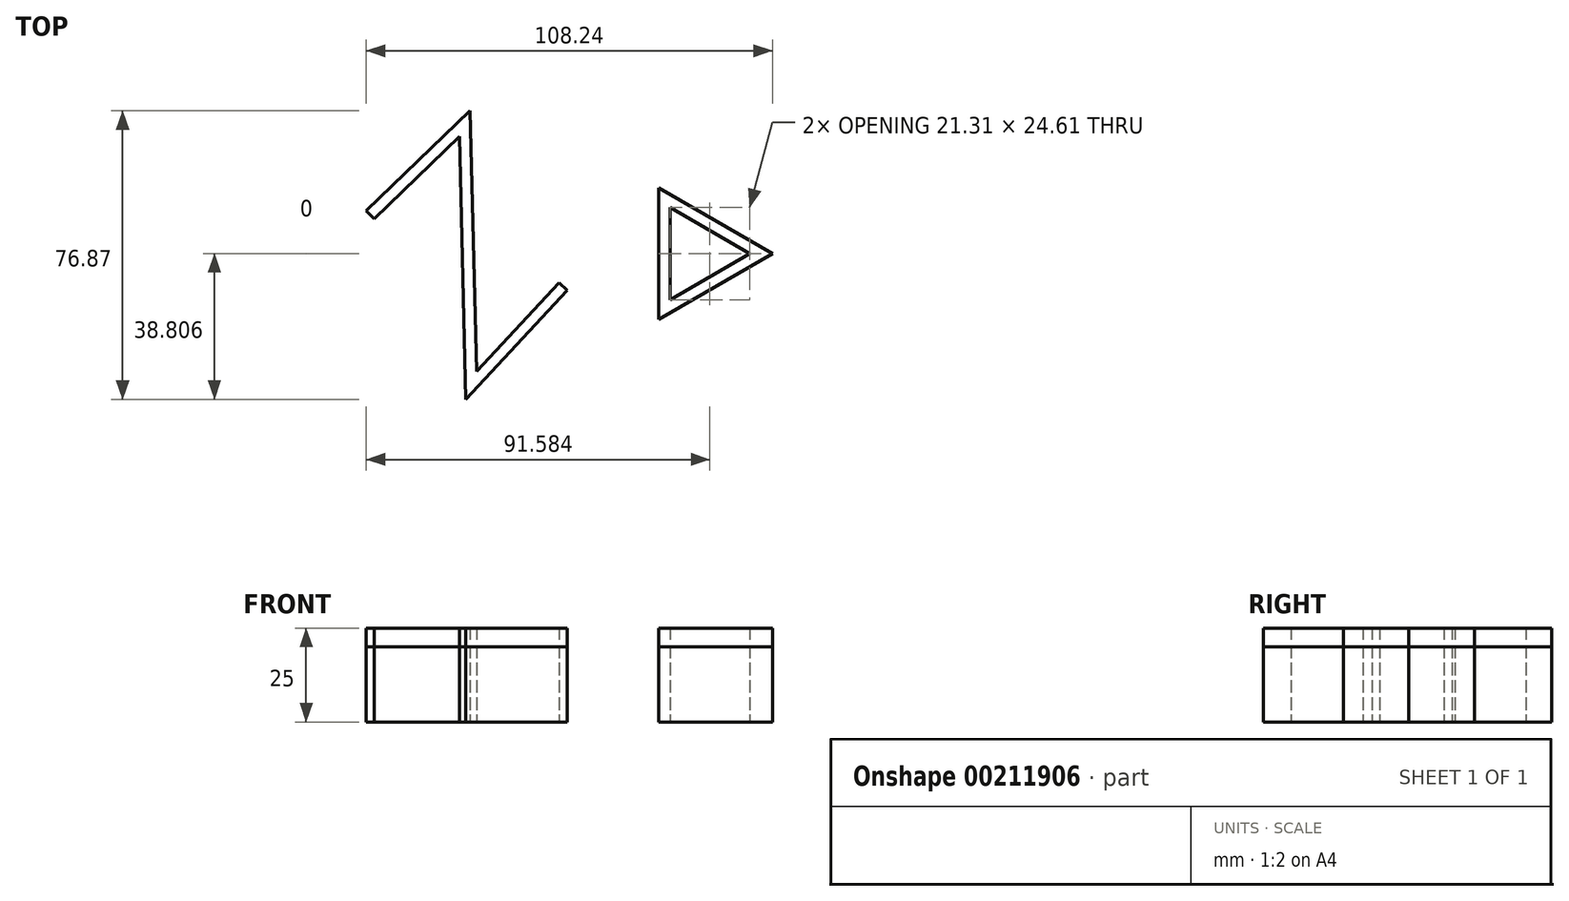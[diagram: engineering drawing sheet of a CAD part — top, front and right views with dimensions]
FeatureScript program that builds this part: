
annotation { "Feature Type Name" : "Feature", "Feature Type Description" : "" }
export const myFeature = defineFeature(function(context is Context, id is Id, definition is map)
    precondition{}
    {
        {
            var Q0;
            Q0=qCreatedBy(makeId("Top.planeOp"),FACE);
            var sketch = newSketch(context, id + "F0", { "sketchPlane" : qUnion([Q0])});
            skCircle(sketch, "E0.cCircle", {"center": v(33.51, 1.03) * mm, "radius": 10.1 * mm, "construction": true});
            skLineSegment(sketch, "E0.0", {"start": v(53.72, 1.03) * mm, "end": v(23.4, -16.47) * mm});
            skLineSegment(sketch, "E0.1", {"start": v(23.4, -16.47) * mm, "end": v(23.4, 18.53) * mm});
            skLineSegment(sketch, "E0.2", {"start": v(23.4, 18.53) * mm, "end": v(53.72, 1.03) * mm});
            skPoint(sketch, "E0.0.midPoint", {"position": v(38.56, -7.72) * mm});
            skLineSegment(sketch, "E1.0", {"start": v(26.4, -11.28) * mm, "end": v(26.4, 13.33) * mm});
            skLineSegment(sketch, "E1.1", {"start": v(47.72, 1.03) * mm, "end": v(26.4, -11.28) * mm});
            skLineSegment(sketch, "E1.2", {"start": v(26.4, 13.33) * mm, "end": v(47.72, 1.03) * mm});
            skLineSegment(sketch, "E2", {"start": v(-53.48, 11.43) * mm, "end": v(-28.28, 35.65) * mm});
            skLineSegment(sketch, "E3", {"start": v(-28.28, 35.65) * mm, "end": v(-26.57, -34.07) * mm});
            skLineSegment(sketch, "E4", {"start": v(-26.57, -34.07) * mm, "end": v(-2.04, -7.79) * mm});
            skLineSegment(sketch, "E5.0", {"start": v(-27.98, -37.78) * mm, "end": v(-0.94, -8.8) * mm});
            skLineSegment(sketch, "E5.1", {"start": v(-29.7, 32.21) * mm, "end": v(-27.98, -37.78) * mm});
            skLineSegment(sketch, "E5.2", {"start": v(-52.44, 10.35) * mm, "end": v(-29.7, 32.21) * mm});
            skLineSegment(sketch, "E6.0", {"start": v(-25.16, -30.36) * mm, "end": v(-3.14, -6.76) * mm});
            skLineSegment(sketch, "E6.1", {"start": v(-26.86, 39.1) * mm, "end": v(-25.16, -30.36) * mm});
            skLineSegment(sketch, "E6.2", {"start": v(-54.52, 12.51) * mm, "end": v(-26.86, 39.1) * mm});
            skLineSegment(sketch, "E7", {"start": v(-54.52, 12.51) * mm, "end": v(-52.44, 10.35) * mm});
            skLineSegment(sketch, "E8", {"start": v(-3.14, -6.76) * mm, "end": v(-0.94, -8.8) * mm});
            skSolve(sketch);
        }
        {
            var Q0;
            Q0 = qSketchRegion(id + "F0", true);
            extrude(context, id + "F1", {"entities" : qUnion([Q0]), "depth" : 20 * mm});
        }
        {
            var Q0;
            Q0 = qSketchRegion(id + "F0", true);
            extrude(context, id + "F2", {"entities" : qUnion([Q0]), "depth" : 25 * mm});
        }
    });
